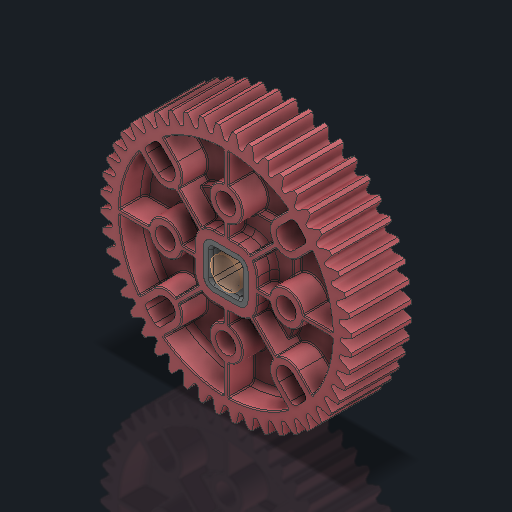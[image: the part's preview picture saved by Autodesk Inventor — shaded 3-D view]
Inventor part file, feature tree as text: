
AUTODESK INVENTOR PART (.ipt)
format: ipt  version: 2023.2 (Build 272271030, 271C)  size: 4,144,128 bytes
history: native  units: in
note: dims shown in document units (in); Inventor stores cm internally (conversion verified against a paired STEP export)
features: other x6, sketch x1
ambient origin geometry x8: Origin, YZ Plane, XZ Plane, XY Plane, X Axis, Y Axis, Z Axis, Center Point
bodies: Solid1 (feature_tree), Solid2 (feature_tree)
feature tree (7):
  other  "HS 48T Gear, No Insert.ipt"
  other  "Solid1::HS 48T Gear, No Insert.ipt"
  other  "Solid2::HS 48T Gear, No Insert.ipt"
  other  "TaggingFeature1"
  sketch  "Sketch1"  dims[d0=0.3937in]
  other  "Srf1"
  other  "Srf1::Derived"
